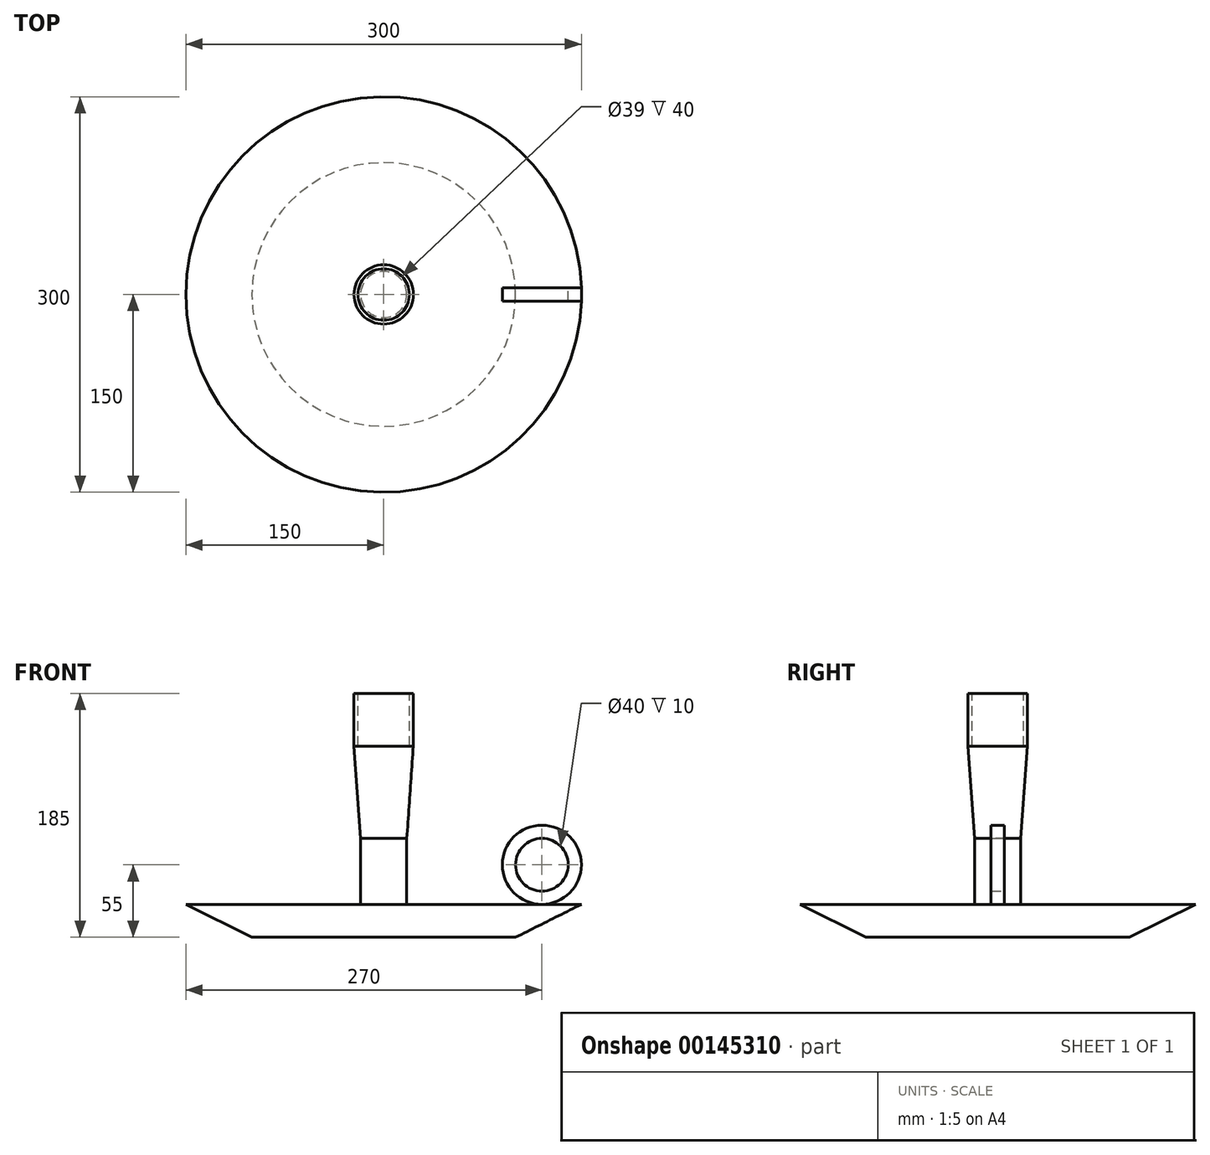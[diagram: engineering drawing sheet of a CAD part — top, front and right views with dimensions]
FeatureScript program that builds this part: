
annotation { "Feature Type Name" : "Feature", "Feature Type Description" : "" }
export const myFeature = defineFeature(function(context is Context, id is Id, definition is map)
    precondition{}
    {
        {
            var Q0;
            Q0=qCreatedBy(makeId("Front.planeOp"),FACE);
            var sketch = newSketch(context, id + "F0", { "sketchPlane" : qUnion([Q0])});
            skLineSegment(sketch, "E0.bottom", {"start": v(17.5, 25) * mm, "end": v(-17.5, 25) * mm});
            skLineSegment(sketch, "E0.top", {"start": v(17.5, -25) * mm, "end": v(-17.5, -25) * mm});
            skLineSegment(sketch, "E0.left", {"start": v(17.5, 25) * mm, "end": v(17.5, -25) * mm});
            skLineSegment(sketch, "E0.right", {"start": v(-17.5, 25) * mm, "end": v(-17.5, -25) * mm});
            skPoint(sketch, "E0.middle", {"position": v(0, 0) * mm});
            skLineSegment(sketch, "E1.bottom", {"start": v(22.5, 135) * mm, "end": v(-22.5, 135) * mm});
            skLineSegment(sketch, "E1.top", {"start": v(22.5, 95) * mm, "end": v(-22.5, 95) * mm});
            skLineSegment(sketch, "E1.left", {"start": v(22.5, 135) * mm, "end": v(22.5, 95) * mm});
            skLineSegment(sketch, "E1.right", {"start": v(-22.5, 135) * mm, "end": v(-22.5, 95) * mm});
            skPoint(sketch, "E1.middle", {"position": v(0, 115) * mm});
            skPoint(sketch, "E1.middle.positionSnap0", {"position": v(0, 25) * mm});
            skPoint(sketch, "E1.centerSnap0", {"position": v(0, 25) * mm});
            skLineSegment(sketch, "E2", {"start": v(-150, -25) * mm, "end": v(150, -25) * mm});
            skLineSegment(sketch, "E3", {"start": v(150, -25) * mm, "end": v(100, -50) * mm});
            skLineSegment(sketch, "E4", {"start": v(100, -50) * mm, "end": v(-100, -50) * mm});
            skLineSegment(sketch, "E5", {"start": v(-100, -50) * mm, "end": v(-150, -25) * mm});
            skLineSegment(sketch, "E6", {"start": v(-22.5, 95) * mm, "end": v(-17.5, 25) * mm});
            skLineSegment(sketch, "E7", {"start": v(22.5, 95) * mm, "end": v(17.5, 25) * mm});
            skCircle(sketch, "E8", {"center": v(120, 5) * mm, "radius": 30 * mm});
            skCircle(sketch, "E9", {"center": v(120, 5) * mm, "radius": 20 * mm});
            skLineSegment(sketch, "E10", {"start": v(0, 135) * mm, "end": v(0, -50) * mm});
            skLineSegment(sketch, "E11.bottom", {"start": v(19.5, 135) * mm, "end": v(-19.5, 135) * mm});
            skLineSegment(sketch, "E11.top", {"start": v(19.5, 95) * mm, "end": v(-19.5, 95) * mm});
            skLineSegment(sketch, "E11.left", {"start": v(19.5, 135) * mm, "end": v(19.5, 95) * mm});
            skLineSegment(sketch, "E11.right", {"start": v(-19.5, 135) * mm, "end": v(-19.5, 95) * mm});
            skSolve(sketch);
        }
        {
            var Q0;
            {var subQ0=sQuery(id+"F0.wireOp",EDGE,"E1.left");Q0=makeQuery(id+"F0.imprint","IMPRINT",FACE,{"disambiguationData":[TD([[makeQuery(id+"F0.imprint","IMPRINT",EDGE,{"derivedFrom":subQ0}),-1.0]])]});}
            var Q1;
            {var subQ5=sQuery(id+"F0.wireOp",EDGE,"E7");Q1=makeQuery(id+"F0.imprint","IMPRINT",FACE,{"disambiguationData":[TD([[makeQuery(id+"F0.imprint","IMPRINT",EDGE,{"derivedFrom":subQ5}),-1.0]])]});}
            var Q2;
            {var subQ0=sQuery(id+"F0.wireOp",EDGE,"E0.left");Q2=makeQuery(id+"F0.imprint","IMPRINT",FACE,{"disambiguationData":[TD([[makeQuery(id+"F0.imprint","IMPRINT",EDGE,{"derivedFrom":subQ0}),-1.0]])]});}
            var Q3;
            {var subQ0=sQuery(id+"F0.wireOp",EDGE,"E3");Q3=makeQuery(id+"F0.imprint","IMPRINT",FACE,{"disambiguationData":[TD([[makeQuery(id+"F0.imprint","IMPRINT",EDGE,{"derivedFrom":subQ0}),-1.0]])]});}
            var Q4;
            Q4=sQuery(id+"F0.wireOp",EDGE,"E10");
            revolve(context, id + "F1", {"entities" : qUnion([Q0, Q1, Q2, Q3]), "axis" : qUnion([Q4]), "revolveType" : RevolveType.FULL});
        }
        {
            var Q0;
            Q0=makeQuery(id+"F0.imprint","IMPRINT",FACE,{"disambiguationData":[TD([[makeQuery(id+"F0.imprint","IMPRINT",EDGE,{"derivedFrom":sQuery(id+"F0.wireOp",EDGE,"E8")}),1.0]])]});
            extrude(context, id + "F2", {"entities" : qUnion([Q0]), "operationType" : NewBodyOperationType.ADD, "endBound" : BoundingType.SYMMETRIC, "depth" : 10 * mm});
        }
    });
